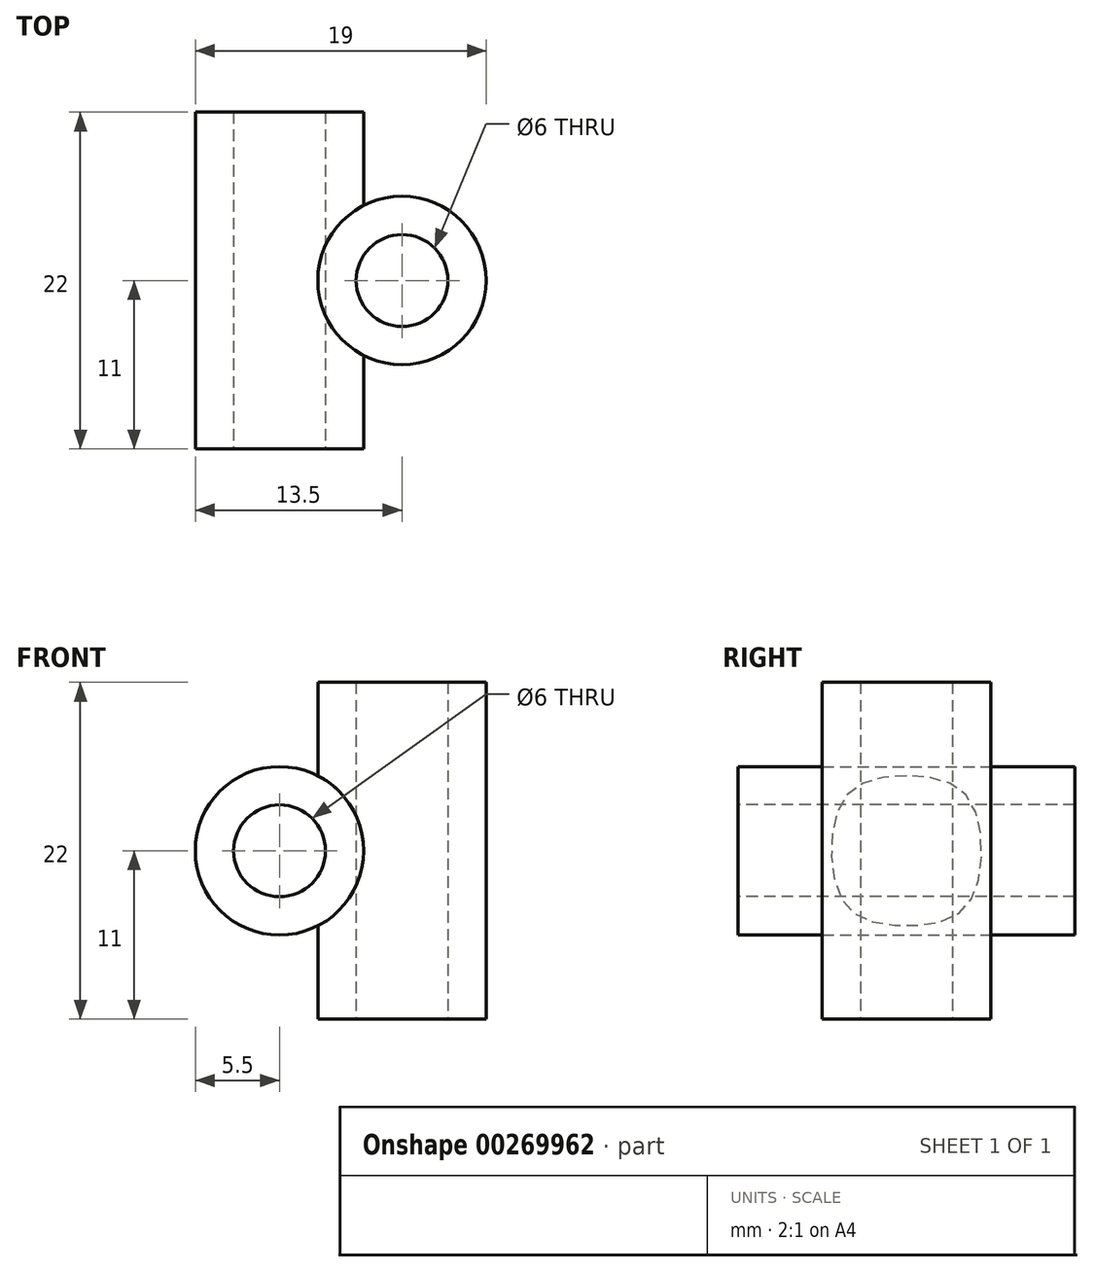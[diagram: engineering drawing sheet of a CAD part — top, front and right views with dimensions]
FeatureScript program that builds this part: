
annotation { "Feature Type Name" : "Feature", "Feature Type Description" : "" }
export const myFeature = defineFeature(function(context is Context, id is Id, definition is map)
    precondition{}
    {
        {
            var Q0;
            Q0=qCreatedBy(makeId("Front.planeOp"),FACE);
            var sketch = newSketch(context, id + "F0", { "sketchPlane" : qUnion([Q0])});
            skCircle(sketch, "E0", {"center": v(0, 0) * mm, "radius": 5.5 * mm});
            skCircle(sketch, "E1", {"center": v(0, 0) * mm, "radius": 3 * mm});
            skSolve(sketch);
        }
        {
            var Q0;
            Q0=makeQuery(id+"F0.imprint","IMPRINT",FACE,{"disambiguationData":[TD([[makeQuery(id+"F0.imprint","IMPRINT",EDGE,{"derivedFrom":sQuery(id+"F0.wireOp",EDGE,"E1")}),1.0]])]});
            var Q1;
            Q1=makeQuery(id+"F0.imprint","IMPRINT",FACE,{"disambiguationData":[TD([[makeQuery(id+"F0.imprint","IMPRINT",EDGE,{"derivedFrom":sQuery(id+"F0.wireOp",EDGE,"E0")}),1.0]])]});
            extrude(context, id + "F1", {"entities" : qUnion([Q0, Q1]), "endBound" : BoundingType.SYMMETRIC, "depth" : 22 * mm});
        }
        {
            var Q0;
            Q0=qCreatedBy(makeId("Top.planeOp"),FACE);
            var sketch = newSketch(context, id + "F2", { "sketchPlane" : qUnion([Q0])});
            skCircle(sketch, "E2", {"center": v(8, 0) * mm, "radius": 5.5 * mm});
            skCircle(sketch, "E3", {"center": v(8, 0) * mm, "radius": 3 * mm});
            skSolve(sketch);
        }
        {
            var Q0;
            Q0=makeQuery(id+"F2.imprint","IMPRINT",FACE,{"disambiguationData":[TD([[makeQuery(id+"F2.imprint","IMPRINT",EDGE,{"derivedFrom":sQuery(id+"F2.wireOp",EDGE,"E3")}),1.0]])]});
            var Q1;
            Q1=makeQuery(id+"F2.imprint","IMPRINT",FACE,{"disambiguationData":[TD([[makeQuery(id+"F2.imprint","IMPRINT",EDGE,{"derivedFrom":sQuery(id+"F2.wireOp",EDGE,"E2")}),1.0]])]});
            extrude(context, id + "F3", {"entities" : qUnion([Q0, Q1]), "operationType" : NewBodyOperationType.ADD, "endBound" : BoundingType.SYMMETRIC, "depth" : 22 * mm});
        }
        {
            var Q0;
            Q0=qCreatedBy(makeId("Front.planeOp"),FACE);
            var sketch = newSketch(context, id + "F4", { "sketchPlane" : qUnion([Q0])});
            skCircle(sketch, "E4.0", {"center": v(0, 0) * mm, "radius": 3 * mm});
            skSolve(sketch);
        }
        {
            var Q0;
            Q0=qSketchRegion(id+"F4",true);
            extrude(context, id + "F5", {"entities" : qUnion([Q0]), "operationType" : NewBodyOperationType.REMOVE, "endBound" : BoundingType.SYMMETRIC, "oppositeDirection" : true, "depth" : 25 * mm});
        }
        {
            var Q0;
            Q0=makeQuery(id+"F3.opExtrude","CAP_FACE",FACE,{"disambiguationData":[OSD([sQuery(id+"F2.wireOp",EDGE,"E2")])],"isStart":true});
            var sketch = newSketch(context, id + "F6", { "sketchPlane" : qUnion([Q0])});
            skCircle(sketch, "E5.0", {"center": v(8, 0) * mm, "radius": 3 * mm});
            skSolve(sketch);
        }
        {
            var Q0;
            Q0=qSketchRegion(id+"F6",true);
            extrude(context, id + "F7", {"entities" : qUnion([Q0]), "operationType" : NewBodyOperationType.REMOVE, "endBound" : BoundingType.THROUGH_ALL, "oppositeDirection" : true, "depth" : 25 * mm});
        }
    });
